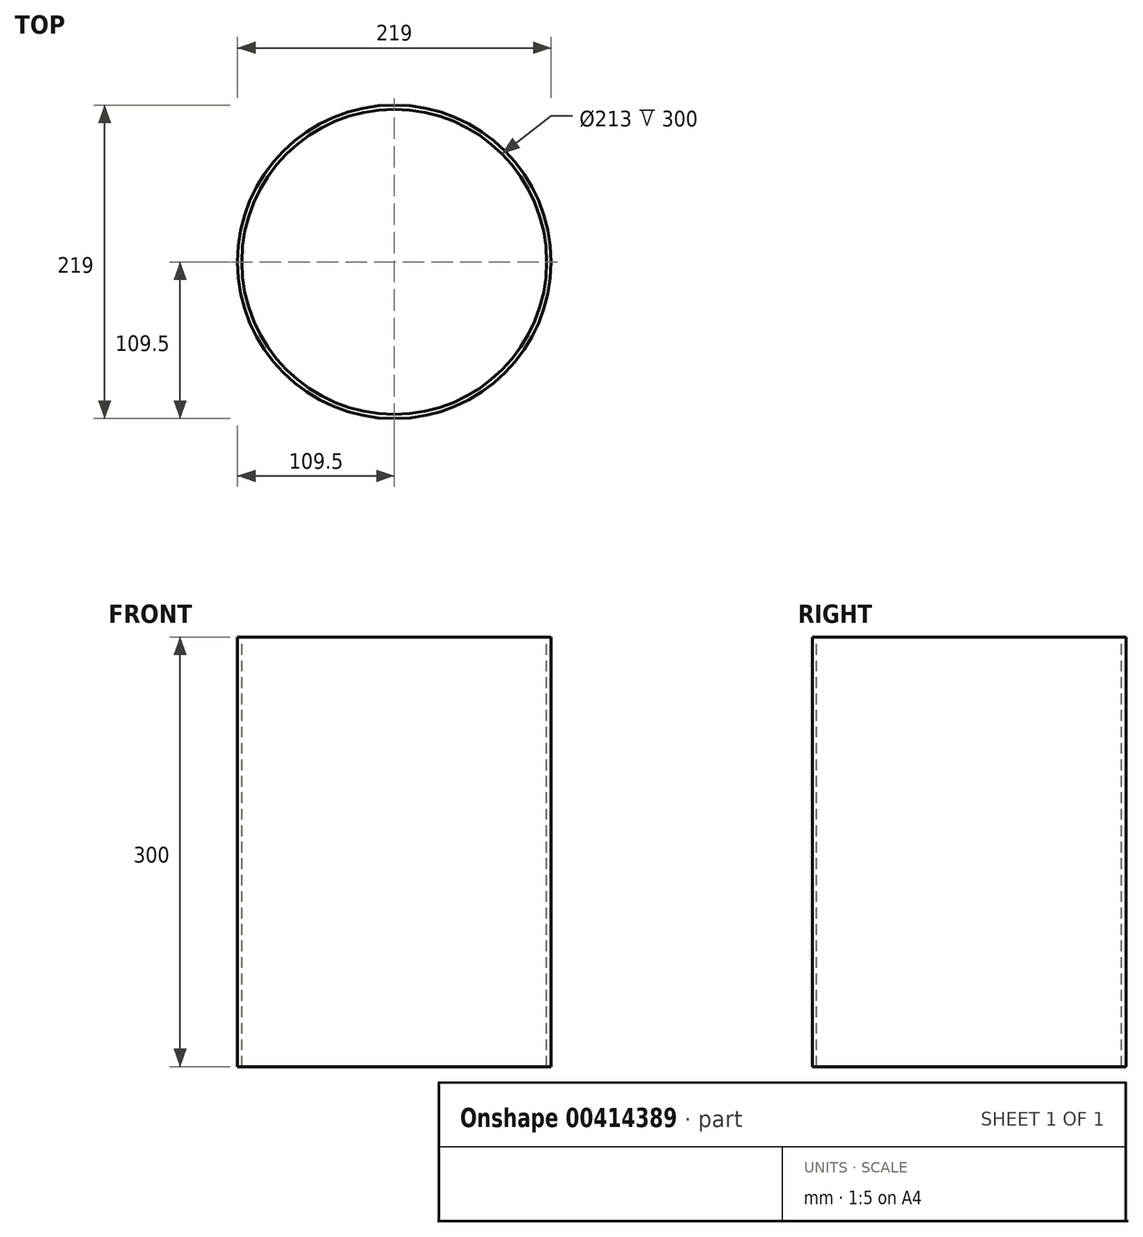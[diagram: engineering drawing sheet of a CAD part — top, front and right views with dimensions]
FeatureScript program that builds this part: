
annotation { "Feature Type Name" : "Feature", "Feature Type Description" : "" }
export const myFeature = defineFeature(function(context is Context, id is Id, definition is map)
    precondition{}
    {
        {
            var Q0;
            Q0=qCreatedBy(makeId("Top.planeOp"),FACE);
            var sketch = newSketch(context, id + "F0", { "sketchPlane" : qUnion([Q0])});
            skCircle(sketch, "E0", {"center": v(0, 0) * mm, "radius": 106.5 * mm});
            skCircle(sketch, "E1.0", {"center": v(0, 0) * mm, "radius": 109.5 * mm});
            skSolve(sketch);
        }
        {
            var Q0;
            Q0 = qSketchRegion(id + "F0", true);
            extrude(context, id + "F1", {"entities" : qUnion([Q0]), "oppositeDirection" : true, "offsetDistance" : 25 * mm, "depth" : 300 * mm});
        }
    });
